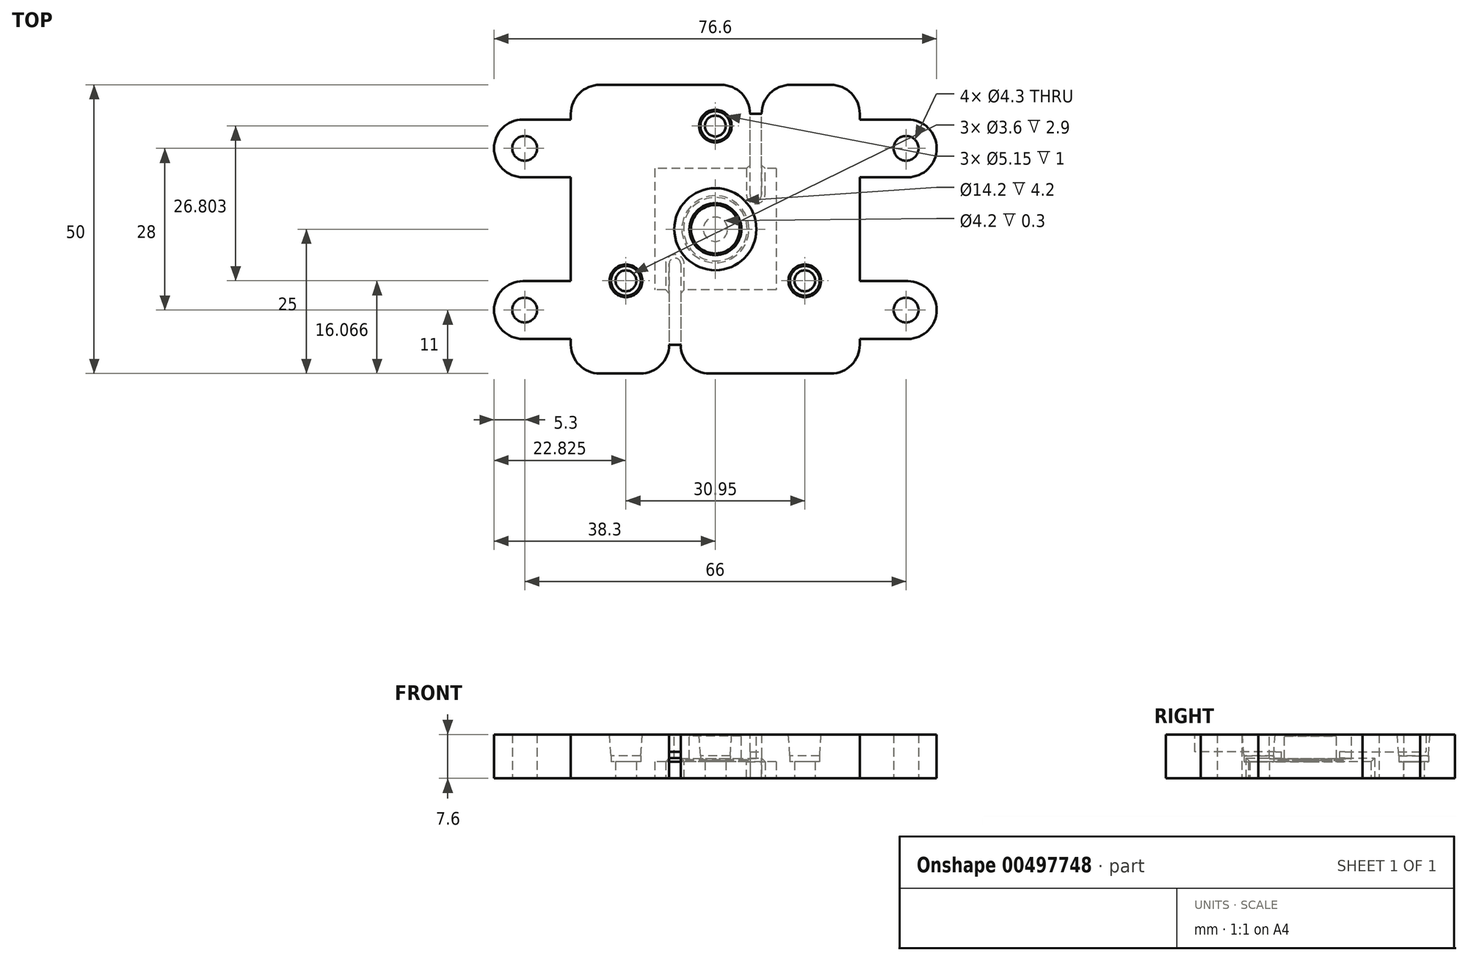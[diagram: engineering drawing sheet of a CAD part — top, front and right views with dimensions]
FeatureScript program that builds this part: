
annotation { "Feature Type Name" : "Feature", "Feature Type Description" : "" }
export const myFeature = defineFeature(function(context is Context, id is Id, definition is map)
    precondition{}
    {
        {
            var Q0;
            Q0=qCreatedBy(makeId("Top.planeOp"),FACE);
            var sketch = newSketch(context, id + "F0", { "sketchPlane" : qUnion([Q0])});
            skLineSegment(sketch, "E0.bottom", {"start": v(10.5, 10.5) * mm, "end": v(-10.5, 10.5) * mm});
            skLineSegment(sketch, "E0.top", {"start": v(10.5, -10.5) * mm, "end": v(-10.5, -10.5) * mm});
            skLineSegment(sketch, "E0.left", {"start": v(10.5, 10.5) * mm, "end": v(10.5, -10.5) * mm});
            skLineSegment(sketch, "E0.right", {"start": v(-10.5, 10.5) * mm, "end": v(-10.5, -10.5) * mm});
            skPoint(sketch, "E0.middle", {"position": v(0, 0) * mm});
            skLineSegment(sketch, "E1.bottom", {"start": v(25, 25) * mm, "end": v(-25, 25) * mm});
            skLineSegment(sketch, "E1.top", {"start": v(25, -25) * mm, "end": v(-25, -25) * mm});
            skLineSegment(sketch, "E1.left", {"start": v(25, 25) * mm, "end": v(25, -25) * mm});
            skLineSegment(sketch, "E1.right", {"start": v(-25, 25) * mm, "end": v(-25, -25) * mm});
            skCircle(sketch, "E2", {"center": v(-15.48, -8.93) * mm, "radius": 1.8 * mm});
            skCircle(sketch, "E3", {"center": v(0, 17.87) * mm, "radius": 1.8 * mm});
            skCircle(sketch, "E4", {"center": v(15.47, -8.93) * mm, "radius": 1.8 * mm});
            skLineSegment(sketch, "E5", {"start": v(-15.48, -8.93) * mm, "end": v(0, 17.87) * mm, "construction": true});
            skLineSegment(sketch, "E6", {"start": v(15.48, -8.93) * mm, "end": v(0, 17.87) * mm, "construction": true});
            skLineSegment(sketch, "E7", {"start": v(15.47, -8.93) * mm, "end": v(-15.48, -8.93) * mm, "construction": true});
            skCircle(sketch, "E8", {"center": v(0, 0) * mm, "radius": 17.87 * mm, "construction": true});
            skLineSegment(sketch, "E9.bottom", {"start": v(-25, 19) * mm, "end": v(-38.3, 19) * mm});
            skLineSegment(sketch, "E9.top", {"start": v(-25, 9) * mm, "end": v(-38.3, 9) * mm});
            skLineSegment(sketch, "E9.left", {"start": v(-25, 19) * mm, "end": v(-25, 9) * mm});
            skLineSegment(sketch, "E9.right", {"start": v(-38.3, 19) * mm, "end": v(-38.3, 9) * mm});
            skCircle(sketch, "E10", {"center": v(-33, 14) * mm, "radius": 2.15 * mm});
            skPoint(sketch, "E10.centerSnap0", {"position": v(-38.3, 14) * mm});
            skLineSegment(sketch, "E11.MirrorCS", {"start": v(38.3, 19) * mm, "end": v(38.3, 9) * mm});
            skLineSegment(sketch, "E12.MirrorCS", {"start": v(25, 19) * mm, "end": v(38.3, 19) * mm});
            skLineSegment(sketch, "E13.MirrorCS", {"start": v(25, 9) * mm, "end": v(38.3, 9) * mm});
            skCircle(sketch, "E14.MirrorC", {"center": v(33, 14) * mm, "radius": 2.15 * mm});
            skLineSegment(sketch, "E15.MirrorCS", {"start": v(-25, -9) * mm, "end": v(-38.3, -9) * mm});
            skLineSegment(sketch, "E16.MirrorCS", {"start": v(-25, -19) * mm, "end": v(-38.3, -19) * mm});
            skCircle(sketch, "E17.MirrorC", {"center": v(-33, -14) * mm, "radius": 2.15 * mm});
            skLineSegment(sketch, "E18.MirrorCS", {"start": v(25, -9) * mm, "end": v(38.3, -9) * mm});
            skLineSegment(sketch, "E19.MirrorCS", {"start": v(38.3, -19) * mm, "end": v(38.3, -9) * mm});
            skLineSegment(sketch, "E20.MirrorCS", {"start": v(25, -19) * mm, "end": v(38.3, -19) * mm});
            skCircle(sketch, "E21.MirrorC", {"center": v(33, -14) * mm, "radius": 2.15 * mm});
            skLineSegment(sketch, "E22.MirrorCS", {"start": v(-38.3, -19) * mm, "end": v(-38.3, -9) * mm});
            skLineSegment(sketch, "E23", {"start": v(6, 10.5) * mm, "end": v(6, 5) * mm});
            skLineSegment(sketch, "E24", {"start": v(6, 5) * mm, "end": v(8, 5) * mm});
            skLineSegment(sketch, "E25", {"start": v(8, 5) * mm, "end": v(8, 10.5) * mm});
            skLineSegment(sketch, "E26", {"start": v(-8, -10.5) * mm, "end": v(-8, -5) * mm});
            skLineSegment(sketch, "E27", {"start": v(-8, -5) * mm, "end": v(-6, -5) * mm});
            skLineSegment(sketch, "E28", {"start": v(-6, -5) * mm, "end": v(-6, -10.5) * mm});
            skLineSegment(sketch, "E29", {"start": v(6, 10.5) * mm, "end": v(6, 25) * mm});
            skLineSegment(sketch, "E30", {"start": v(8, 10.5) * mm, "end": v(8, 25) * mm});
            skLineSegment(sketch, "E31", {"start": v(-8, -10.5) * mm, "end": v(-8, -25) * mm});
            skLineSegment(sketch, "E32", {"start": v(-6, -10.5) * mm, "end": v(-6, -25) * mm});
            skCircle(sketch, "E33", {"center": v(0, 0) * mm, "radius": 5.5 * mm});
            skSolve(sketch);
        }
        {
            var Q0;
            {var subQ9=sQuery(id+"F0.wireOp",EDGE,"E0.right");Q0=makeQuery(id+"F0.imprint","IMPRINT",FACE,{"disambiguationData":[TD([[makeQuery(id+"F0.imprint","IMPRINT",EDGE,{"derivedFrom":subQ9}),-1.0]])]});}
            var Q1;
            {var subQ8=sQuery(id+"F0.wireOp",EDGE,"E0.left");Q1=makeQuery(id+"F0.imprint","IMPRINT",FACE,{"disambiguationData":[TD([[makeQuery(id+"F0.imprint","IMPRINT",EDGE,{"derivedFrom":subQ8}),1.0]])]});}
            var Q2;
            Q2=makeQuery(id+"F0.imprint","IMPRINT",FACE,{"disambiguationData":[TD([[makeQuery(id+"F0.imprint","IMPRINT",EDGE,{"derivedFrom":sQuery(id+"F0.wireOp",EDGE,"E9.bottom")}),1.0]])]});
            var Q3;
            {var subQ0=sQuery(id+"F0.wireOp",EDGE,"E15.MirrorCS");Q3=makeQuery(id+"F0.imprint","IMPRINT",FACE,{"disambiguationData":[TD([[makeQuery(id+"F0.imprint","IMPRINT",EDGE,{"derivedFrom":subQ0}),1.0]])]});}
            var Q4;
            {var subQ1=sQuery(id+"F0.wireOp",EDGE,"E18.MirrorCS");Q4=makeQuery(id+"F0.imprint","IMPRINT",FACE,{"disambiguationData":[TD([[makeQuery(id+"F0.imprint","IMPRINT",EDGE,{"derivedFrom":subQ1}),-1.0]])]});}
            var Q5;
            Q5=makeQuery(id+"F0.imprint","IMPRINT",FACE,{"disambiguationData":[TD([[makeQuery(id+"F0.imprint","IMPRINT",EDGE,{"derivedFrom":sQuery(id+"F0.wireOp",EDGE,"E11.MirrorCS")}),-1.0]])]});
            extrude(context, id + "F1", {"entities" : qUnion([Q0, Q1, Q2, Q3, Q4, Q5]), "depth" : 7.9 * mm, "offsetDistance" : 25 * mm});
        }
        {
            var Q0;
            Q0=makeQuery(id+"F1.opExtrude","CAP_FACE",FACE,{"disambiguationData":[OSD([sQuery(id+"F0.wireOp",EDGE,"E0.bottom"),sQuery(id+"F0.wireOp",EDGE,"E0.top"),sQuery(id+"F0.wireOp",EDGE,"E0.right"),sQuery(id+"F0.wireOp",EDGE,"E1.bottom"),sQuery(id+"F0.wireOp",EDGE,"E1.top"),sQuery(id+"F0.wireOp",EDGE,"E1.right"),sQuery(id+"F0.wireOp",EDGE,"E2"),sQuery(id+"F0.wireOp",EDGE,"E3"),sQuery(id+"F0.wireOp",EDGE,"E9.bottom"),sQuery(id+"F0.wireOp",EDGE,"E9.top"),sQuery(id+"F0.wireOp",EDGE,"E9.right"),sQuery(id+"F0.wireOp",EDGE,"E10"),sQuery(id+"F0.wireOp",EDGE,"E15.MirrorCS"),sQuery(id+"F0.wireOp",EDGE,"E16.MirrorCS"),sQuery(id+"F0.wireOp",EDGE,"E17.MirrorC"),sQuery(id+"F0.wireOp",EDGE,"E22.MirrorCS"),sQuery(id+"F0.wireOp",EDGE,"E29"),sQuery(id+"F0.wireOp",EDGE,"E31")])],"isStart":false});
            var sketch = newSketch(context, id + "F2", { "sketchPlane" : qUnion([Q0])});
            skCircle(sketch, "E34.0", {"center": v(0, 0) * mm, "radius": 5.5 * mm});
            skLineSegment(sketch, "E35.0", {"start": v(25, 25) * mm, "end": v(-25, 25) * mm});
            skLineSegment(sketch, "E35.1", {"start": v(-25, 25) * mm, "end": v(-25, -25) * mm});
            skLineSegment(sketch, "E35.2", {"start": v(25, 25) * mm, "end": v(25, -25) * mm});
            skLineSegment(sketch, "E35.3", {"start": v(25, -25) * mm, "end": v(-25, -25) * mm});
            skLineSegment(sketch, "E36.0", {"start": v(-6, -10.5) * mm, "end": v(-6, -25) * mm});
            skLineSegment(sketch, "E36.1", {"start": v(-8, -10.5) * mm, "end": v(-8, -25) * mm});
            skLineSegment(sketch, "E36.2", {"start": v(-8, -10.5) * mm, "end": v(-8, -5) * mm});
            skLineSegment(sketch, "E36.3", {"start": v(-8, -5) * mm, "end": v(-6, -5) * mm});
            skLineSegment(sketch, "E36.4", {"start": v(-6, -5) * mm, "end": v(-6, -10.5) * mm});
            skLineSegment(sketch, "E36.5", {"start": v(6, 10.5) * mm, "end": v(6, 5) * mm});
            skLineSegment(sketch, "E36.6", {"start": v(6, 5) * mm, "end": v(8, 5) * mm});
            skLineSegment(sketch, "E36.7", {"start": v(8, 5) * mm, "end": v(8, 10.5) * mm});
            skLineSegment(sketch, "E36.8", {"start": v(6, 10.5) * mm, "end": v(6, 25) * mm});
            skLineSegment(sketch, "E36.9", {"start": v(8, 10.5) * mm, "end": v(8, 25) * mm});
            skLineSegment(sketch, "E37.0", {"start": v(25, -9) * mm, "end": v(38.3, -9) * mm});
            skLineSegment(sketch, "E37.1", {"start": v(38.3, -19) * mm, "end": v(38.3, -9) * mm});
            skLineSegment(sketch, "E37.2", {"start": v(38.3, 19) * mm, "end": v(38.3, 9) * mm});
            skLineSegment(sketch, "E37.3", {"start": v(25, 19) * mm, "end": v(38.3, 19) * mm});
            skLineSegment(sketch, "E37.4", {"start": v(25, 9) * mm, "end": v(38.3, 9) * mm});
            skLineSegment(sketch, "E37.5", {"start": v(25, -19) * mm, "end": v(38.3, -19) * mm});
            skCircle(sketch, "E38.0", {"center": v(33, 14) * mm, "radius": 2.15 * mm});
            skCircle(sketch, "E38.1", {"center": v(33, -14) * mm, "radius": 2.15 * mm});
            skPoint(sketch, "E39.0", {"position": v(0, 17.87) * mm});
            skPoint(sketch, "E39.1", {"position": v(-15.48, -8.93) * mm});
            skPoint(sketch, "E39.2", {"position": v(15.48, -8.93) * mm});
            skCircle(sketch, "E40", {"center": v(0, 17.87) * mm, "radius": 2.58 * mm});
            skCircle(sketch, "E41", {"center": v(-15.48, -8.93) * mm, "radius": 2.58 * mm});
            skCircle(sketch, "E42", {"center": v(15.48, -8.93) * mm, "radius": 2.58 * mm});
            skSolve(sketch);
        }
        {
            var Q0;
            {var subQ6=sQuery(id+"F2.wireOp",EDGE,"E36.1");Q0=makeQuery(id+"F2.imprint","IMPRINT",FACE,{"disambiguationData":[TD([[makeQuery(id+"F2.imprint","IMPRINT",EDGE,{"derivedFrom":subQ6}),-1.0]])]});}
            var Q1;
            Q1=makeQuery(id+"F2.imprint","IMPRINT",FACE,{"disambiguationData":[TD([[makeQuery(id+"F2.imprint","IMPRINT",EDGE,{"derivedFrom":sQuery(id+"F2.wireOp",EDGE,"E34.0")}),-1.0]])]});
            var Q2;
            {var subQ1=makeQuery(id+"F1.opExtrude","CAP_EDGE",EDGE,{"disambiguationData":[OSD([sQuery(id+"F0.wireOp",EDGE,"E15.MirrorCS")])],"isStart":false});Q2=makeQuery(id+"F2.imprint","IMPRINT",FACE,{"disambiguationData":[TD([[makeQuery(id+"F2.imprint","IMPRINT",EDGE,{"derivedFrom":subQ1}),1.0]])]});}
            var Q3;
            {var subQ0=makeQuery(id+"F1.opExtrude","CAP_EDGE",EDGE,{"disambiguationData":[OSD([sQuery(id+"F0.wireOp",EDGE,"E9.bottom")])],"isStart":false});Q3=makeQuery(id+"F2.imprint","IMPRINT",FACE,{"disambiguationData":[TD([[makeQuery(id+"F2.imprint","IMPRINT",EDGE,{"derivedFrom":subQ0}),1.0]])]});}
            var Q4;
            Q4=makeQuery(id+"F2.imprint","IMPRINT",FACE,{"disambiguationData":[TD([[makeQuery(id+"F2.imprint","IMPRINT",EDGE,{"derivedFrom":sQuery(id+"F2.wireOp",EDGE,"E37.2")}),-1.0]])]});
            var Q5;
            {var subQ0=sQuery(id+"F2.wireOp",EDGE,"E37.0");Q5=makeQuery(id+"F2.imprint","IMPRINT",FACE,{"disambiguationData":[TD([[makeQuery(id+"F2.imprint","IMPRINT",EDGE,{"derivedFrom":subQ0}),-1.0]])]});}
            extrude(context, id + "F3", {"entities" : qUnion([Q0, Q1, Q2, Q3, Q4, Q5]), "operationType" : NewBodyOperationType.ADD, "depth" : 4.7 * mm, "offsetDistance" : 25 * mm});
        }
        {
            var Q0;
            Q0=makeQuery(id+"F3.opExtrude","SWEPT_EDGE",EDGE,{"disambiguationData":[OSD([sQuery(id+"F2.wireOp",EDGE,"E36.3"),sQuery(id+"F2.wireOp",EDGE,"E36.4")])]});
            var Q1;
            Q1=makeQuery(id+"F3.opExtrude","SWEPT_EDGE",EDGE,{"disambiguationData":[OSD([sQuery(id+"F2.wireOp",EDGE,"E36.2"),sQuery(id+"F2.wireOp",EDGE,"E36.3")])]});
            var Q2;
            Q2=makeQuery(id+"F3.opExtrude","SWEPT_EDGE",EDGE,{"disambiguationData":[OSD([sQuery(id+"F2.wireOp",EDGE,"E36.5"),sQuery(id+"F2.wireOp",EDGE,"E36.6")])]});
            var Q3;
            Q3=makeQuery(id+"F3.opExtrude","SWEPT_EDGE",EDGE,{"disambiguationData":[OSD([sQuery(id+"F2.wireOp",EDGE,"E36.6"),sQuery(id+"F2.wireOp",EDGE,"E36.7")])]});
            fillet(context, id + "F4", {"entities" : qUnion([Q0, Q1, Q2, Q3]), "radius" : 1 * mm, "tangentPropagation" : true, "allowEdgeOverflow" : false});
        }
        {
            var Q0;
            Q0=makeQuery(id+"F1.opExtrude","SWEPT_EDGE",EDGE,{"disambiguationData":[OSD([sQuery(id+"F0.wireOp",EDGE,"E9.top"),sQuery(id+"F0.wireOp",EDGE,"E9.right")])]});
            var Q1;
            Q1=makeQuery(id+"F1.opExtrude","SWEPT_EDGE",EDGE,{"disambiguationData":[OSD([sQuery(id+"F0.wireOp",EDGE,"E9.bottom"),sQuery(id+"F0.wireOp",EDGE,"E9.right")])]});
            var Q2;
            Q2=makeQuery(id+"F1.opExtrude","SWEPT_EDGE",EDGE,{"disambiguationData":[OSD([sQuery(id+"F0.wireOp",EDGE,"E16.MirrorCS"),sQuery(id+"F0.wireOp",EDGE,"E22.MirrorCS")])]});
            var Q3;
            Q3=makeQuery(id+"F1.opExtrude","SWEPT_EDGE",EDGE,{"disambiguationData":[OSD([sQuery(id+"F0.wireOp",EDGE,"E15.MirrorCS"),sQuery(id+"F0.wireOp",EDGE,"E22.MirrorCS")])]});
            var Q4;
            Q4=makeQuery(id+"F1.opExtrude","SWEPT_EDGE",EDGE,{"disambiguationData":[OSD([sQuery(id+"F0.wireOp",EDGE,"E19.MirrorCS"),sQuery(id+"F0.wireOp",EDGE,"E20.MirrorCS")])]});
            var Q5;
            Q5=makeQuery(id+"F1.opExtrude","SWEPT_EDGE",EDGE,{"disambiguationData":[OSD([sQuery(id+"F0.wireOp",EDGE,"E18.MirrorCS"),sQuery(id+"F0.wireOp",EDGE,"E19.MirrorCS")])]});
            var Q6;
            Q6=makeQuery(id+"F1.opExtrude","SWEPT_EDGE",EDGE,{"disambiguationData":[OSD([sQuery(id+"F0.wireOp",EDGE,"E11.MirrorCS"),sQuery(id+"F0.wireOp",EDGE,"E13.MirrorCS")])]});
            var Q7;
            Q7=makeQuery(id+"F1.opExtrude","SWEPT_EDGE",EDGE,{"disambiguationData":[OSD([sQuery(id+"F0.wireOp",EDGE,"E11.MirrorCS"),sQuery(id+"F0.wireOp",EDGE,"E12.MirrorCS")])]});
            var Q8;
            Q8=makeQuery(id+"F3.boolean.opBoolean","MERGE",EDGE,{"derivedFrom":[makeQuery(id+"F1.opExtrude","SWEPT_EDGE",EDGE,{"disambiguationData":[OSD([sQuery(id+"F0.wireOp",EDGE,"E1.top"),sQuery(id+"F0.wireOp",EDGE,"E1.right")])]}),makeQuery(id+"F3.opExtrude","SWEPT_EDGE",EDGE,{"disambiguationData":[OSD([sQuery(id+"F2.wireOp",EDGE,"E35.1"),sQuery(id+"F2.wireOp",EDGE,"E35.3")])]})]});
            var Q9;
            Q9=makeQuery(id+"F3.boolean.opBoolean","MERGE",EDGE,{"derivedFrom":[makeQuery(id+"F1.opExtrude","SWEPT_EDGE",EDGE,{"disambiguationData":[OSD([sQuery(id+"F0.wireOp",EDGE,"E1.top"),sQuery(id+"F0.wireOp",EDGE,"E1.left")])]}),makeQuery(id+"F3.opExtrude","SWEPT_EDGE",EDGE,{"disambiguationData":[OSD([sQuery(id+"F2.wireOp",EDGE,"E35.2"),sQuery(id+"F2.wireOp",EDGE,"E35.3")])]})]});
            var Q10;
            Q10=makeQuery(id+"F3.boolean.opBoolean","MERGE",EDGE,{"derivedFrom":[makeQuery(id+"F1.opExtrude","SWEPT_EDGE",EDGE,{"disambiguationData":[OSD([sQuery(id+"F0.wireOp",EDGE,"E1.bottom"),sQuery(id+"F0.wireOp",EDGE,"E1.left")])]}),makeQuery(id+"F3.opExtrude","SWEPT_EDGE",EDGE,{"disambiguationData":[OSD([sQuery(id+"F2.wireOp",EDGE,"E35.0"),sQuery(id+"F2.wireOp",EDGE,"E35.2")])]})]});
            var Q11;
            Q11=makeQuery(id+"F3.boolean.opBoolean","MERGE",EDGE,{"derivedFrom":[makeQuery(id+"F1.opExtrude","SWEPT_EDGE",EDGE,{"disambiguationData":[OSD([sQuery(id+"F0.wireOp",EDGE,"E1.bottom"),sQuery(id+"F0.wireOp",EDGE,"E1.right")])]}),makeQuery(id+"F3.opExtrude","SWEPT_EDGE",EDGE,{"disambiguationData":[OSD([sQuery(id+"F2.wireOp",EDGE,"E35.0"),sQuery(id+"F2.wireOp",EDGE,"E35.1")])]})]});
            var Q12;
            Q12=makeQuery(id+"F3.boolean.opBoolean","MERGE",EDGE,{"derivedFrom":[makeQuery(id+"F1.opExtrude","SWEPT_EDGE",EDGE,{"disambiguationData":[OSD([sQuery(id+"F0.wireOp",EDGE,"E1.bottom"),sQuery(id+"F0.wireOp",EDGE,"E29")])]}),makeQuery(id+"F3.opExtrude","SWEPT_EDGE",EDGE,{"disambiguationData":[OSD([sQuery(id+"F2.wireOp",EDGE,"E35.0"),sQuery(id+"F2.wireOp",EDGE,"E36.8")])]})]});
            var Q13;
            Q13=makeQuery(id+"F3.boolean.opBoolean","MERGE",EDGE,{"derivedFrom":[makeQuery(id+"F1.opExtrude","SWEPT_EDGE",EDGE,{"disambiguationData":[OSD([sQuery(id+"F0.wireOp",EDGE,"E1.bottom"),sQuery(id+"F0.wireOp",EDGE,"E30")])]}),makeQuery(id+"F3.opExtrude","SWEPT_EDGE",EDGE,{"disambiguationData":[OSD([sQuery(id+"F2.wireOp",EDGE,"E35.0"),sQuery(id+"F2.wireOp",EDGE,"E36.9")])]})]});
            var Q14;
            Q14=makeQuery(id+"F3.boolean.opBoolean","MERGE",EDGE,{"derivedFrom":[makeQuery(id+"F1.opExtrude","SWEPT_EDGE",EDGE,{"disambiguationData":[OSD([sQuery(id+"F0.wireOp",EDGE,"E1.top"),sQuery(id+"F0.wireOp",EDGE,"E31")])]}),makeQuery(id+"F3.opExtrude","SWEPT_EDGE",EDGE,{"disambiguationData":[OSD([sQuery(id+"F2.wireOp",EDGE,"E35.3"),sQuery(id+"F2.wireOp",EDGE,"E36.1")])]})]});
            var Q15;
            Q15=makeQuery(id+"F3.boolean.opBoolean","MERGE",EDGE,{"derivedFrom":[makeQuery(id+"F1.opExtrude","SWEPT_EDGE",EDGE,{"disambiguationData":[OSD([sQuery(id+"F0.wireOp",EDGE,"E1.top"),sQuery(id+"F0.wireOp",EDGE,"E32")])]}),makeQuery(id+"F3.opExtrude","SWEPT_EDGE",EDGE,{"disambiguationData":[OSD([sQuery(id+"F2.wireOp",EDGE,"E35.3"),sQuery(id+"F2.wireOp",EDGE,"E36.0")])]})]});
            fillet(context, id + "F5", {"entities" : qUnion([Q0, Q1, Q2, Q3, Q4, Q5, Q6, Q7, Q8, Q9, Q10, Q11, Q12, Q13, Q14, Q15]), "radius" : 5 * mm, "tangentPropagation" : true, "allowEdgeOverflow" : false});
        }
        {
            var Q0;
            Q0=makeQuery(id+"F1.opExtrude","CAP_EDGE",EDGE,{"disambiguationData":[OSD([sQuery(id+"F0.wireOp",EDGE,"E0.right")])],"isStart":true});
            var Q1;
            {var subQ0=sQuery(id+"F0.wireOp",EDGE,"E0.top");Q1=makeQuery(id+"F1.opExtrude","CAP_EDGE",EDGE,{"disambiguationData":[OSD([subQ0]),TDD([makeQuery(id+"F0.imprint","IMPRINT",EDGE,{"disambiguationData":[TD([[makeQuery(id+"F0.imprint","INTERSECT",VERTEX,{"derivedFrom":[subQ0,sQuery(id+"F0.wireOp",EDGE,"E0.right")]}),1.0]])],"derivedFrom":subQ0})])],"isStart":true});}
            var Q2;
            {var subQ0=sQuery(id+"F0.wireOp",EDGE,"E0.top");Q2=makeQuery(id+"F1.opExtrude","CAP_EDGE",EDGE,{"disambiguationData":[OSD([subQ0]),TDD([makeQuery(id+"F0.imprint","IMPRINT",EDGE,{"disambiguationData":[TD([[makeQuery(id+"F0.imprint","INTERSECT",VERTEX,{"derivedFrom":[subQ0,sQuery(id+"F0.wireOp",EDGE,"E0.left")]}),-1.0]])],"derivedFrom":subQ0})])],"isStart":true});}
            var Q3;
            Q3=makeQuery(id+"F1.opExtrude","CAP_EDGE",EDGE,{"disambiguationData":[OSD([sQuery(id+"F0.wireOp",EDGE,"E0.left")])],"isStart":true});
            var Q4;
            {var subQ0=sQuery(id+"F0.wireOp",EDGE,"E0.bottom");Q4=makeQuery(id+"F1.opExtrude","CAP_EDGE",EDGE,{"disambiguationData":[OSD([subQ0]),TDD([makeQuery(id+"F0.imprint","IMPRINT",EDGE,{"disambiguationData":[TD([[makeQuery(id+"F0.imprint","INTERSECT",VERTEX,{"derivedFrom":[subQ0,sQuery(id+"F0.wireOp",EDGE,"E0.left")]}),-1.0]])],"derivedFrom":subQ0})])],"isStart":true});}
            var Q5;
            {var subQ0=sQuery(id+"F0.wireOp",EDGE,"E0.bottom");Q5=makeQuery(id+"F1.opExtrude","CAP_EDGE",EDGE,{"disambiguationData":[OSD([subQ0]),TDD([makeQuery(id+"F0.imprint","IMPRINT",EDGE,{"disambiguationData":[TD([[makeQuery(id+"F0.imprint","INTERSECT",VERTEX,{"derivedFrom":[subQ0,sQuery(id+"F0.wireOp",EDGE,"E0.right")]}),1.0]])],"derivedFrom":subQ0})])],"isStart":true});}
            var Q6;
            Q6=makeQuery(id+"F3.opExtrude","CAP_EDGE",EDGE,{"disambiguationData":[OSD([sQuery(id+"F2.wireOp",EDGE,"E36.0"),sQuery(id+"F2.wireOp",EDGE,"E36.4")])],"isStart":true});
            var Q7;
            Q7=makeQuery(id+"F3.opExtrude","CAP_EDGE",EDGE,{"disambiguationData":[OSD([sQuery(id+"F2.wireOp",EDGE,"E36.7"),sQuery(id+"F2.wireOp",EDGE,"E36.9")])],"isStart":true});
            var Q8;
            Q8=makeQuery(id+"F1.opExtrude","SWEPT_EDGE",EDGE,{"disambiguationData":[OSD([sQuery(id+"F0.wireOp",EDGE,"E0.top"),sQuery(id+"F0.wireOp",EDGE,"E26"),sQuery(id+"F0.wireOp",EDGE,"E31")])]});
            var Q9;
            Q9=makeQuery(id+"F1.opExtrude","SWEPT_EDGE",EDGE,{"disambiguationData":[OSD([sQuery(id+"F0.wireOp",EDGE,"E0.top"),sQuery(id+"F0.wireOp",EDGE,"E28"),sQuery(id+"F0.wireOp",EDGE,"E32")])]});
            var Q10;
            Q10=makeQuery(id+"F1.opExtrude","SWEPT_EDGE",EDGE,{"disambiguationData":[OSD([sQuery(id+"F0.wireOp",EDGE,"E0.bottom"),sQuery(id+"F0.wireOp",EDGE,"E23"),sQuery(id+"F0.wireOp",EDGE,"E29")])]});
            var Q11;
            Q11=makeQuery(id+"F1.opExtrude","SWEPT_EDGE",EDGE,{"disambiguationData":[OSD([sQuery(id+"F0.wireOp",EDGE,"E0.bottom"),sQuery(id+"F0.wireOp",EDGE,"E25"),sQuery(id+"F0.wireOp",EDGE,"E30")])]});
            chamfer(context, id + "F6", {"entities" : qUnion([Q0, Q1, Q2, Q3, Q4, Q5, Q6, Q7, Q8, Q9, Q10, Q11]), "width" : 0.6 * mm, "tangentPropagation" : true});
        }
        {
            var Q0;
            Q0=makeQuery(id+"F3.opExtrude","CAP_EDGE",EDGE,{"disambiguationData":[OSD([sQuery(id+"F2.wireOp",EDGE,"E40")])],"isStart":false});
            var Q1;
            Q1=makeQuery(id+"F3.opExtrude","CAP_EDGE",EDGE,{"disambiguationData":[OSD([sQuery(id+"F2.wireOp",EDGE,"E42")])],"isStart":false});
            var Q2;
            Q2=makeQuery(id+"F3.opExtrude","CAP_EDGE",EDGE,{"disambiguationData":[OSD([sQuery(id+"F2.wireOp",EDGE,"E41")])],"isStart":false});
            chamfer(context, id + "F7", {"entities" : qUnion([Q0, Q1, Q2]), "chamferType" : ChamferType.TWO_OFFSETS, "width1" : 3.7 * mm, "oppositeDirection" : false, "width2" : 0.25 * mm, "tangentPropagation" : true});
        }
        {
            var Q0;
            {var subQ9=sQuery(id+"F0.wireOp",EDGE,"E0.right");Q0=makeQuery(id+"F0.imprint","IMPRINT",FACE,{"disambiguationData":[TD([[makeQuery(id+"F0.imprint","IMPRINT",EDGE,{"derivedFrom":subQ9}),-1.0]])]});}
            var Q1;
            {var subQ8=sQuery(id+"F0.wireOp",EDGE,"E0.left");Q1=makeQuery(id+"F0.imprint","IMPRINT",FACE,{"disambiguationData":[TD([[makeQuery(id+"F0.imprint","IMPRINT",EDGE,{"derivedFrom":subQ8}),1.0]])]});}
            var Q2;
            {var subQ0=sQuery(id+"F0.wireOp",EDGE,"E15.MirrorCS");Q2=makeQuery(id+"F0.imprint","IMPRINT",FACE,{"disambiguationData":[TD([[makeQuery(id+"F0.imprint","IMPRINT",EDGE,{"derivedFrom":subQ0}),1.0]])]});}
            var Q3;
            Q3=makeQuery(id+"F0.imprint","IMPRINT",FACE,{"disambiguationData":[TD([[makeQuery(id+"F0.imprint","IMPRINT",EDGE,{"derivedFrom":sQuery(id+"F0.wireOp",EDGE,"E9.bottom")}),1.0]])]});
            var Q4;
            Q4=makeQuery(id+"F0.imprint","IMPRINT",FACE,{"disambiguationData":[TD([[makeQuery(id+"F0.imprint","IMPRINT",EDGE,{"derivedFrom":sQuery(id+"F0.wireOp",EDGE,"E11.MirrorCS")}),-1.0]])]});
            var Q5;
            {var subQ1=sQuery(id+"F0.wireOp",EDGE,"E18.MirrorCS");Q5=makeQuery(id+"F0.imprint","IMPRINT",FACE,{"disambiguationData":[TD([[makeQuery(id+"F0.imprint","IMPRINT",EDGE,{"derivedFrom":subQ1}),-1.0]])]});}
            extrude(context, id + "F8", {"entities" : qUnion([Q0, Q1, Q2, Q3, Q4, Q5]), "operationType" : NewBodyOperationType.REMOVE, "depth" : 5 * mm, "offsetDistance" : 25 * mm});
        }
        {
            var Q0;
            Q0=makeQuery(id+"F3.opExtrude","CAP_FACE",FACE,{"disambiguationData":[OSD([sQuery(id+"F0.wireOp",EDGE,"E9.bottom"),sQuery(id+"F0.wireOp",EDGE,"E9.top"),sQuery(id+"F0.wireOp",EDGE,"E9.right"),sQuery(id+"F0.wireOp",EDGE,"E10"),sQuery(id+"F0.wireOp",EDGE,"E15.MirrorCS"),sQuery(id+"F0.wireOp",EDGE,"E16.MirrorCS"),sQuery(id+"F0.wireOp",EDGE,"E17.MirrorC"),sQuery(id+"F0.wireOp",EDGE,"E22.MirrorCS"),sQuery(id+"F2.wireOp",EDGE,"E34.0"),sQuery(id+"F2.wireOp",EDGE,"E35.0"),sQuery(id+"F2.wireOp",EDGE,"E35.1"),sQuery(id+"F2.wireOp",EDGE,"E35.2"),sQuery(id+"F2.wireOp",EDGE,"E35.3"),sQuery(id+"F2.wireOp",EDGE,"E36.0"),sQuery(id+"F2.wireOp",EDGE,"E36.1"),sQuery(id+"F2.wireOp",EDGE,"E36.2"),sQuery(id+"F2.wireOp",EDGE,"E36.3"),sQuery(id+"F2.wireOp",EDGE,"E36.4"),sQuery(id+"F2.wireOp",EDGE,"E36.5"),sQuery(id+"F2.wireOp",EDGE,"E36.6"),sQuery(id+"F2.wireOp",EDGE,"E36.7"),sQuery(id+"F2.wireOp",EDGE,"E36.8"),sQuery(id+"F2.wireOp",EDGE,"E36.9"),sQuery(id+"F2.wireOp",EDGE,"E37.0"),sQuery(id+"F2.wireOp",EDGE,"E37.1"),sQuery(id+"F2.wireOp",EDGE,"E37.2"),sQuery(id+"F2.wireOp",EDGE,"E37.3"),sQuery(id+"F2.wireOp",EDGE,"E37.4"),sQuery(id+"F2.wireOp",EDGE,"E37.5"),sQuery(id+"F2.wireOp",EDGE,"E38.0"),sQuery(id+"F2.wireOp",EDGE,"E38.1"),sQuery(id+"F2.wireOp",EDGE,"E40"),sQuery(id+"F2.wireOp",EDGE,"E41"),sQuery(id+"F2.wireOp",EDGE,"E42")])],"isStart":false});
            var sketch = newSketch(context, id + "F9", { "sketchPlane" : qUnion([Q0])});
            skPoint(sketch, "E43.0", {"position": v(0, 0) * mm});
            skCircle(sketch, "E44", {"center": v(0, 0) * mm, "radius": 7.1 * mm});
            skCircle(sketch, "E45.0", {"center": v(0, 0) * mm, "radius": 4.5 * mm});
            skSolve(sketch);
        }
        {
            var Q0;
            Q0=makeQuery(id+"F9.imprint","IMPRINT",FACE,{"disambiguationData":[TD([[makeQuery(id+"F9.imprint","IMPRINT",EDGE,{"derivedFrom":sQuery(id+"F9.wireOp",EDGE,"E44")}),1.0]])]});
            extrude(context, id + "F10", {"entities" : qUnion([Q0]), "operationType" : NewBodyOperationType.REMOVE, "oppositeDirection" : true, "depth" : 4.2 * mm, "offsetDistance" : 25 * mm});
        }
        {
            var Q0;
            Q0=makeQuery(id+"F9.imprint","IMPRINT",FACE,{"disambiguationData":[TD([[makeQuery(id+"F9.imprint","IMPRINT",EDGE,{"derivedFrom":sQuery(id+"F9.wireOp",EDGE,"E45.0")}),1.0]])]});
            var Q1;
            Q1=makeQuery(id+"F10.boolean.opBoolean","COPY",FACE,{"derivedFrom":makeQuery(id+"F10.opExtrude","CAP_FACE",FACE,{"disambiguationData":[OSD([sQuery(id+"F2.wireOp",EDGE,"E34.0"),sQuery(id+"F9.wireOp",EDGE,"E44")])],"isStart":false})});
            extrude(context, id + "F11", {"entities" : qUnion([Q0]), "endBound" : BoundingType.UP_TO_SURFACE, "oppositeDirection" : true, "depth" : 4.3 * mm, "endBoundEntityFace" : qUnion([Q1]), "offsetDistance" : 25 * mm});
        }
        {
            var Q0;
            Q0=makeQuery(id+"F3.opExtrude","CAP_EDGE",EDGE,{"disambiguationData":[OSD([sQuery(id+"F2.wireOp",EDGE,"E34.0")])],"isStart":true});
            var Q1;
            Q1=makeQuery(id+"F10.boolean.opBoolean","COPY",EDGE,{"derivedFrom":makeQuery(id+"F10.opExtrude","CAP_EDGE",EDGE,{"disambiguationData":[OSD([sQuery(id+"F9.wireOp",EDGE,"E44")])],"isStart":true})});
            var Q2;
            Q2=makeQuery(id+"F11.opExtrude","CAP_EDGE",EDGE,{"disambiguationData":[OSD([sQuery(id+"F9.wireOp",EDGE,"E45.0")])],"isStart":true});
            chamfer(context, id + "F12", {"entities" : qUnion([Q0, Q1, Q2]), "width" : 0.3 * mm, "tangentPropagation" : true});
        }
        {
            var Q0;
            Q0=makeQuery(id+"F10.boolean.opBoolean","COPY",FACE,{"derivedFrom":makeQuery(id+"F10.opExtrude","CAP_FACE",FACE,{"disambiguationData":[OSD([sQuery(id+"F2.wireOp",EDGE,"E34.0"),sQuery(id+"F9.wireOp",EDGE,"E44")])],"isStart":false})});
            var sketch = newSketch(context, id + "F13", { "sketchPlane" : qUnion([Q0])});
            skCircle(sketch, "E46.0", {"center": v(0, 0) * mm, "radius": 5.5 * mm});
            skCircle(sketch, "E47", {"center": v(0, 0) * mm, "radius": 2.1 * mm});
            skSolve(sketch);
        }
        {
            var Q0;
            Q0=makeQuery(id+"F13.imprint","IMPRINT",FACE,{"disambiguationData":[TD([[makeQuery(id+"F13.imprint","IMPRINT",EDGE,{"derivedFrom":sQuery(id+"F13.wireOp",EDGE,"E46.0")}),1.0]])]});
            extrude(context, id + "F14", {"entities" : qUnion([Q0]), "operationType" : NewBodyOperationType.ADD, "oppositeDirection" : true, "depth" : 0.3 * mm, "offsetDistance" : 25 * mm});
        }
        {
            var Q0;
            Q0=makeQuery(id+"F3.opExtrude","CAP_FACE",FACE,{"disambiguationData":[OSD([sQuery(id+"F0.wireOp",EDGE,"E9.bottom"),sQuery(id+"F0.wireOp",EDGE,"E9.top"),sQuery(id+"F0.wireOp",EDGE,"E9.right"),sQuery(id+"F0.wireOp",EDGE,"E10"),sQuery(id+"F0.wireOp",EDGE,"E15.MirrorCS"),sQuery(id+"F0.wireOp",EDGE,"E16.MirrorCS"),sQuery(id+"F0.wireOp",EDGE,"E17.MirrorC"),sQuery(id+"F0.wireOp",EDGE,"E22.MirrorCS"),sQuery(id+"F2.wireOp",EDGE,"E34.0"),sQuery(id+"F2.wireOp",EDGE,"E35.0"),sQuery(id+"F2.wireOp",EDGE,"E35.1"),sQuery(id+"F2.wireOp",EDGE,"E35.2"),sQuery(id+"F2.wireOp",EDGE,"E35.3"),sQuery(id+"F2.wireOp",EDGE,"E36.0"),sQuery(id+"F2.wireOp",EDGE,"E36.1"),sQuery(id+"F2.wireOp",EDGE,"E36.2"),sQuery(id+"F2.wireOp",EDGE,"E36.3"),sQuery(id+"F2.wireOp",EDGE,"E36.4"),sQuery(id+"F2.wireOp",EDGE,"E36.5"),sQuery(id+"F2.wireOp",EDGE,"E36.6"),sQuery(id+"F2.wireOp",EDGE,"E36.7"),sQuery(id+"F2.wireOp",EDGE,"E36.8"),sQuery(id+"F2.wireOp",EDGE,"E36.9"),sQuery(id+"F2.wireOp",EDGE,"E37.0"),sQuery(id+"F2.wireOp",EDGE,"E37.1"),sQuery(id+"F2.wireOp",EDGE,"E37.2"),sQuery(id+"F2.wireOp",EDGE,"E37.3"),sQuery(id+"F2.wireOp",EDGE,"E37.4"),sQuery(id+"F2.wireOp",EDGE,"E37.5"),sQuery(id+"F2.wireOp",EDGE,"E38.0"),sQuery(id+"F2.wireOp",EDGE,"E38.1"),sQuery(id+"F2.wireOp",EDGE,"E40"),sQuery(id+"F2.wireOp",EDGE,"E41"),sQuery(id+"F2.wireOp",EDGE,"E42")])],"isStart":false});
            var sketch = newSketch(context, id + "F15", { "sketchPlane" : qUnion([Q0])});
            skLineSegment(sketch, "E48.0", {"start": v(-6, -6) * mm, "end": v(-6, -20) * mm});
            skLineSegment(sketch, "E48.1", {"start": v(-8, -6) * mm, "end": v(-8, -20) * mm});
            skArc(sketch, "E48.2", {"start": v(-8, -6) * mm, "mid": v(-7, -5) * mm, "end": v(-6, -6) * mm});
            skLineSegment(sketch, "E48.3", {"start": v(6, 11.1) * mm, "end": v(6, 20) * mm});
            skLineSegment(sketch, "E48.4", {"start": v(6, 6) * mm, "end": v(6, 20) * mm});
            skLineSegment(sketch, "E48.5", {"start": v(8, 6) * mm, "end": v(8, 20) * mm});
            skArc(sketch, "E48.6", {"start": v(8, 6) * mm, "mid": v(7, 5) * mm, "end": v(6, 6) * mm});
            skLineSegment(sketch, "E49", {"start": v(6, 20) * mm, "end": v(8, 20) * mm});
            skLineSegment(sketch, "E50", {"start": v(-8, -20) * mm, "end": v(-6, -20) * mm});
            skSolve(sketch);
        }
        {
            var Q0;
            Q0=makeQuery(id+"F15.imprint","IMPRINT",FACE,{"disambiguationData":[TD([[makeQuery(id+"F15.imprint","IMPRINT",EDGE,{"derivedFrom":sQuery(id+"F15.wireOp",EDGE,"E48.0")}),-1.0]])]});
            var Q1;
            Q1=makeQuery(id+"F15.imprint","IMPRINT",FACE,{"disambiguationData":[TD([[makeQuery(id+"F15.imprint","IMPRINT",EDGE,{"derivedFrom":sQuery(id+"F15.wireOp",EDGE,"E48.5")}),1.0]])]});
            extrude(context, id + "F16", {"entities" : qUnion([Q0, Q1]), "operationType" : NewBodyOperationType.ADD, "oppositeDirection" : true, "depth" : 3 * mm, "offsetDistance" : 25 * mm});
        }
    });
